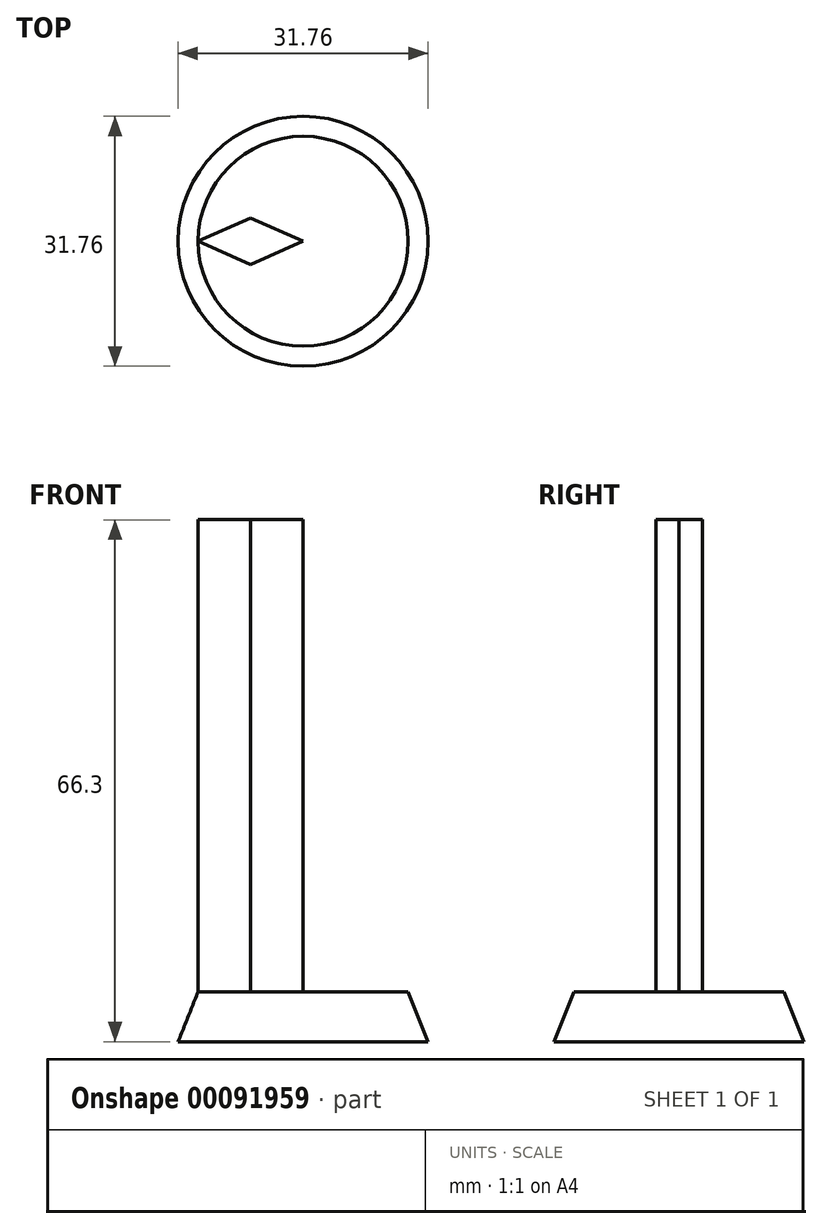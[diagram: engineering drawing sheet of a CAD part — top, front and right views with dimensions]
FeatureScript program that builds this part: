
annotation { "Feature Type Name" : "Feature", "Feature Type Description" : "" }
export const myFeature = defineFeature(function(context is Context, id is Id, definition is map)
    precondition{}
    {
        {
            var Q0;
            Q0=qCreatedBy(makeId("Top.planeOp"),FACE);
            var sketch = newSketch(context, id + "F0", { "sketchPlane" : qUnion([Q0])});
            skCircle(sketch, "E0", {"center": v(0, 0) * mm, "radius": 15.88 * mm});
            skSolve(sketch);
        }
        {
            var Q0;
            Q0 = qSketchRegion(id + "F0", true);
            var Q1;
            Q1=makeQuery(id+"F0.imprint","IMPRINT",FACE,{"disambiguationData":[TD([[makeQuery(id+"F0.imprint","IMPRINT",EDGE,{"derivedFrom":sQuery(id+"F0.wireOp",EDGE,"E0")}),1.0]])]});
            extrude(context, id + "F1", {"entities" : qUnion([Q0, Q1]), "depth" : 6.35 * mm});
        }
        {
            var Q0;
            Q0=makeQuery(id+"F1.opExtrude","CAP_EDGE",EDGE,{"disambiguationData":[OSD([sQuery(id+"F0.wireOp",EDGE,"E0")])],"isStart":false});
            chamfer(context, id + "F2", {"entities" : qUnion([Q0]), "chamferType" : ChamferType.TWO_OFFSETS, "width1" : 2.54 * mm, "oppositeDirection" : false, "width2" : 6.35 * mm});
        }
        {
            var Q0;
            Q0=makeQuery(id+"F1.opExtrude","CAP_FACE",FACE,{"disambiguationData":[OSD([sQuery(id+"F0.wireOp",EDGE,"E0")])],"isStart":false});
            var sketch = newSketch(context, id + "F3", { "sketchPlane" : qUnion([Q0])});
            skLineSegment(sketch, "E1", {"start": v(-13.34, 0) * mm, "end": v(-6.67, 2.95) * mm});
            skLineSegment(sketch, "E2", {"start": v(-6.67, 2.95) * mm, "end": v(0, 0) * mm});
            skLineSegment(sketch, "E3.MirrorCS", {"start": v(-6.67, -2.95) * mm, "end": v(0, 0) * mm});
            skLineSegment(sketch, "E4.MirrorCS", {"start": v(-13.34, 0) * mm, "end": v(-6.67, -2.95) * mm});
            skSolve(sketch);
        }
        {
            var Q0;
            Q0=makeQuery(id+"F3.imprint","IMPRINT",FACE,{"disambiguationData":[TD([[makeQuery(id+"F3.imprint","IMPRINT",EDGE,{"derivedFrom":sQuery(id+"F3.wireOp",EDGE,"E1")}),-1.0]])]});
            extrude(context, id + "F4", {"entities" : qUnion([Q0]), "operationType" : NewBodyOperationType.ADD, "depth" : 59.95 * mm});
        }
    });
